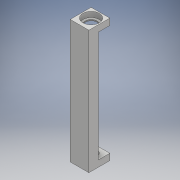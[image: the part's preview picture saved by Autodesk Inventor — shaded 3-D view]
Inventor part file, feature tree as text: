
AUTODESK INVENTOR PART (.ipt)
format: ipt  version: 2018 (Build 220112000, 112)  size: 156,672 bytes
history: native  units: mm
features: extrude x6, sketch x6, fillet x1
ambient origin geometry x8: Origin, YZ Plane, XZ Plane, XY Plane, X Axis, Y Axis, Z Axis, Center Point
bodies: Solid1 (feature_tree)
feature tree (13):
  extrude  "Extrusion1"  Depth=165.0mm
  extrude  "Extrusion2"  Depth=8.5mm
  extrude  "Extrusion3"  Depth=25.0mm TaperAngle=0.0deg
  extrude  "Extrusion4"  Depth=25.0mm
  extrude  "Extrusion5"  Depth=7.1mm
  extrude  "Extrusion6"  Depth=7.1mm TaperAngle=0.0deg
  fillet  "Fillet1"  Radius=5.0mm
  sketch  "Sketch1"  dims[d0=25.0mm d1=165.0mm]
  sketch  "Sketch2"  dims[d2=3.0mm d3=0.0mm d4=8.5mm]
  sketch  "Sketch3"  dims[d5=8.5mm d6=25.0mm d7=0.0mm]
  sketch  "Sketch4"  dims[d8=25.0mm d9=22.0mm]
  sketch  "Sketch5"  dims[d10=7.1mm d11=0.0mm d12=15.5mm]
  sketch  "Sketch6"  dims[d13=165.0mm d14=0.0mm d15=7.1mm d16=0.0mm d17=5.0mm d18=5.0mm d19=10.0mm d20=0.0mm d21=2.0mm]
